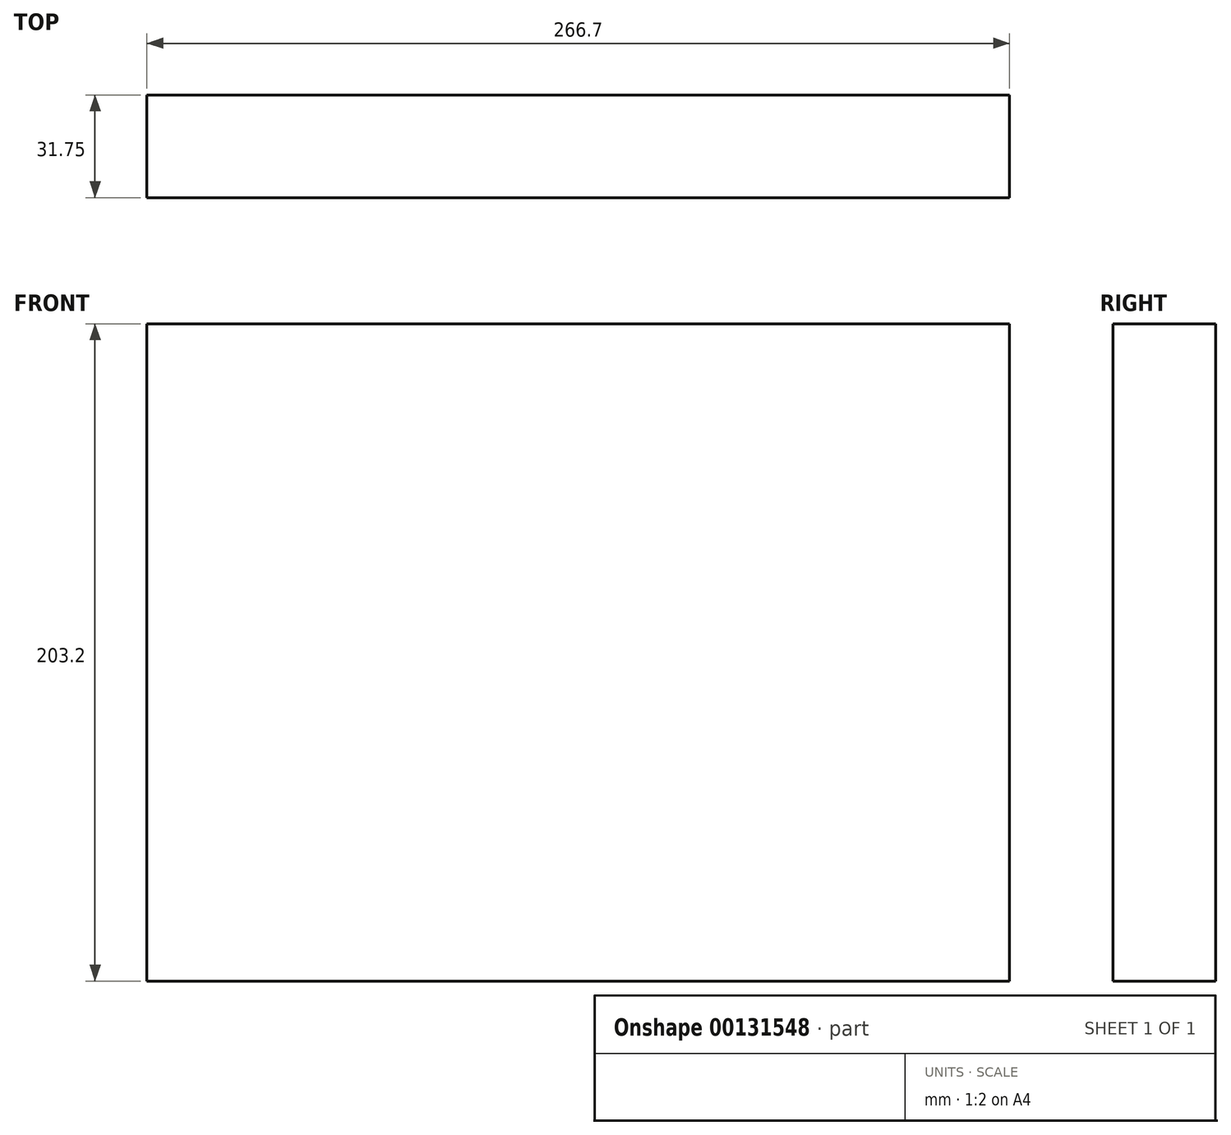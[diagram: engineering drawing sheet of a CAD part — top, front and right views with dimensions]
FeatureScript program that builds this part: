
annotation { "Feature Type Name" : "Feature", "Feature Type Description" : "" }
export const myFeature = defineFeature(function(context is Context, id is Id, definition is map)
    precondition{}
    {
        {
            var Q0;
            Q0=qCreatedBy(makeId("Front.planeOp"),FACE);
            var sketch = newSketch(context, id + "F0", { "sketchPlane" : qUnion([Q0])});
            skLineSegment(sketch, "E0.bottom", {"start": v(133.35, 101.6) * mm, "end": v(-133.35, 101.6) * mm});
            skLineSegment(sketch, "E0.top", {"start": v(133.35, -101.6) * mm, "end": v(-133.35, -101.6) * mm});
            skLineSegment(sketch, "E0.left", {"start": v(133.35, 101.6) * mm, "end": v(133.35, -101.6) * mm});
            skLineSegment(sketch, "E0.right", {"start": v(-133.35, 101.6) * mm, "end": v(-133.35, -101.6) * mm});
            skPoint(sketch, "E0.middle", {"position": v(0, 0) * mm});
            skSolve(sketch);
        }
        {
            var Q0;
            Q0=makeQuery(id+"F0.imprint","IMPRINT",FACE,{"disambiguationData":[TD([[makeQuery(id+"F0.imprint","IMPRINT",EDGE,{"derivedFrom":sQuery(id+"F0.wireOp",EDGE,"E0.bottom")}),1.0]])]});
            extrude(context, id + "F1", {"entities" : qUnion([Q0]), "depth" : 31.75 * mm});
        }
    });
